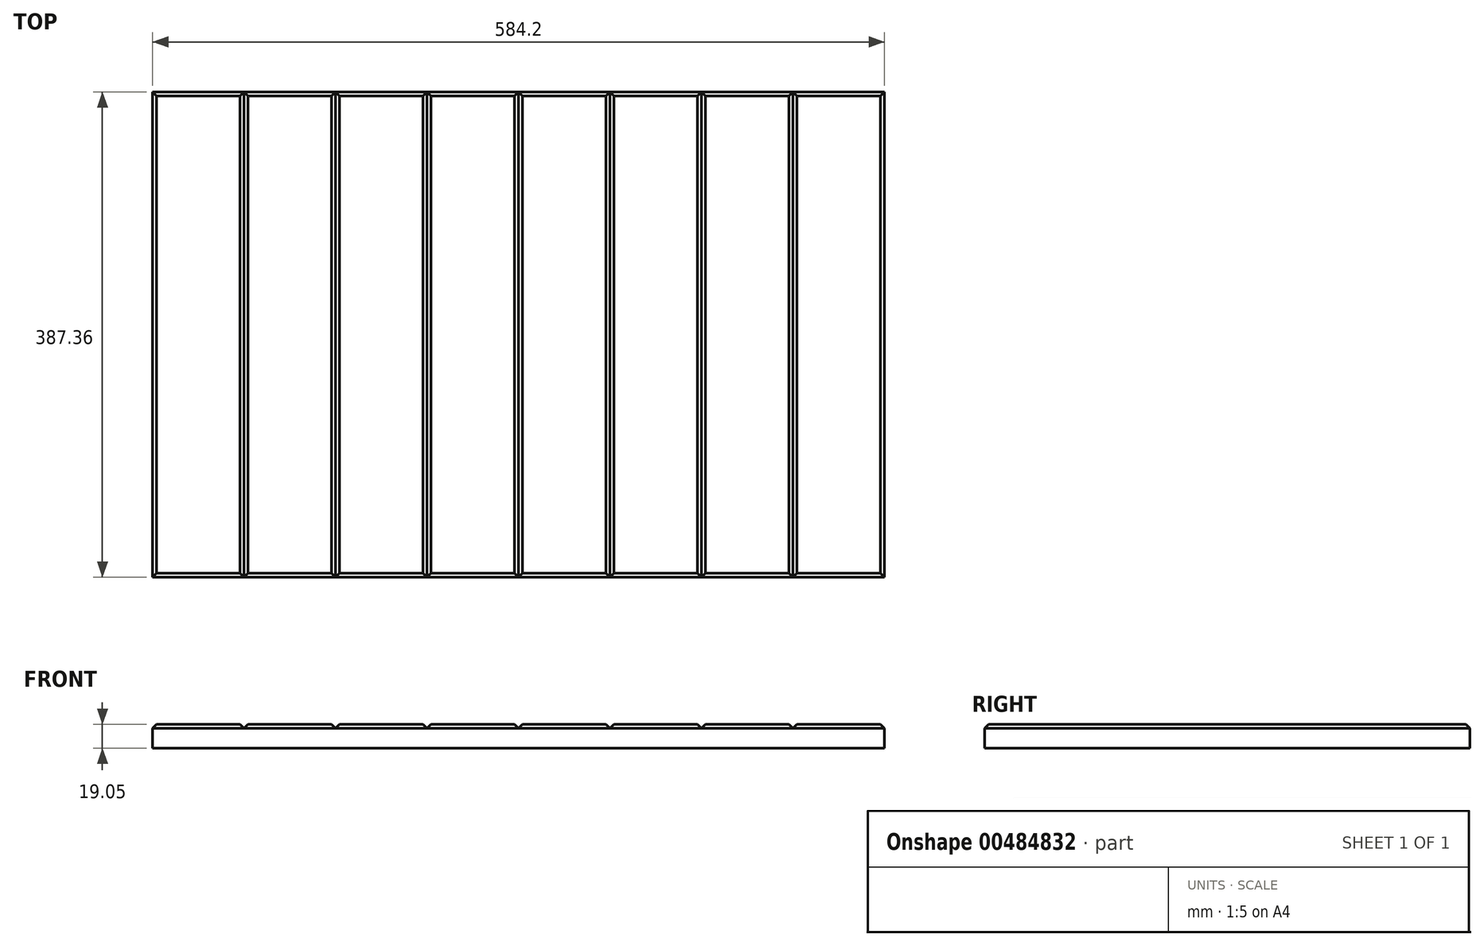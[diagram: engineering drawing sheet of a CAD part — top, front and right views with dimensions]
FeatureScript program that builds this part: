
annotation { "Feature Type Name" : "Feature", "Feature Type Description" : "" }
export const myFeature = defineFeature(function(context is Context, id is Id, definition is map)
    precondition{}
    {
        {
            var Q0;
            Q0=qCreatedBy(makeId("Top.planeOp"),FACE);
            var sketch = newSketch(context, id + "F0", { "sketchPlane" : qUnion([Q0])});
            skLineSegment(sketch, "E0.bottom", {"start": v(-292.1, 193.67) * mm, "end": v(292.1, 193.67) * mm});
            skLineSegment(sketch, "E0.top", {"start": v(-292.1, -193.68) * mm, "end": v(292.1, -193.68) * mm});
            skLineSegment(sketch, "E0.left", {"start": v(-292.1, 193.67) * mm, "end": v(-292.1, -193.68) * mm});
            skLineSegment(sketch, "E0.right", {"start": v(292.1, 193.67) * mm, "end": v(292.1, -193.68) * mm});
            skPoint(sketch, "E0.middle", {"position": v(0, 0) * mm});
            skSolve(sketch);
        }
        {
            var Q0;
            Q0 = qSketchRegion(id + "F0", true);
            extrude(context, id + "F1", {"entities" : qUnion([Q0]), "depth" : 19.05 * mm});
        }
        {
            var Q0;
            Q0=makeQuery(id+"F1.opExtrude","SWEPT_FACE",FACE,{"disambiguationData":[OSD([sQuery(id+"F0.wireOp",EDGE,"E0.top")])]});
            var sketch = newSketch(context, id + "F2", { "sketchPlane" : qUnion([Q0])});
            skLineSegment(sketch, "E1", {"start": v(-292.1, 19.05) * mm, "end": v(-219.08, 19.05) * mm});
            skLineSegment(sketch, "E2", {"start": v(-219.08, 19.05) * mm, "end": v(-222.25, 19.05) * mm});
            skLineSegment(sketch, "E3", {"start": v(-222.25, 19.05) * mm, "end": v(-215.9, 19.05) * mm});
            skLineSegment(sketch, "E4", {"start": v(-219.08, 15.88) * mm, "end": v(-215.9, 19.05) * mm});
            skLineSegment(sketch, "E5", {"start": v(-219.08, 15.87) * mm, "end": v(-222.25, 19.05) * mm});
            skLineSegment(sketch, "E6.1.0.0", {"start": v(-149.23, 19.05) * mm, "end": v(-142.88, 19.05) * mm});
            skLineSegment(sketch, "E6.1.0.1", {"start": v(-146.05, 15.87) * mm, "end": v(-149.23, 19.05) * mm});
            skLineSegment(sketch, "E6.1.0.2", {"start": v(-146.05, 15.88) * mm, "end": v(-142.88, 19.05) * mm});
            skLineSegment(sketch, "E6.1.0.3", {"start": v(-146.05, 19.05) * mm, "end": v(-149.23, 19.05) * mm});
            skLineSegment(sketch, "E6.2.0.0", {"start": v(-76.2, 19.05) * mm, "end": v(-69.85, 19.05) * mm});
            skLineSegment(sketch, "E6.2.0.1", {"start": v(-73.03, 15.87) * mm, "end": v(-76.2, 19.05) * mm});
            skLineSegment(sketch, "E6.2.0.2", {"start": v(-73.03, 15.88) * mm, "end": v(-69.85, 19.05) * mm});
            skLineSegment(sketch, "E6.2.0.3", {"start": v(-73.03, 19.05) * mm, "end": v(-76.2, 19.05) * mm});
            skLineSegment(sketch, "E6.3.0.0", {"start": v(-3.18, 19.05) * mm, "end": v(3.17, 19.05) * mm});
            skLineSegment(sketch, "E6.3.0.1", {"start": v(0, 15.87) * mm, "end": v(-3.18, 19.05) * mm});
            skLineSegment(sketch, "E6.3.0.2", {"start": v(0, 15.88) * mm, "end": v(3.17, 19.05) * mm});
            skLineSegment(sketch, "E6.3.0.3", {"start": v(0, 19.05) * mm, "end": v(-3.18, 19.05) * mm});
            skLineSegment(sketch, "E6.4.0.0", {"start": v(69.85, 19.05) * mm, "end": v(76.2, 19.05) * mm});
            skLineSegment(sketch, "E6.4.0.1", {"start": v(73.03, 15.87) * mm, "end": v(69.85, 19.05) * mm});
            skLineSegment(sketch, "E6.4.0.2", {"start": v(73.03, 15.88) * mm, "end": v(76.2, 19.05) * mm});
            skLineSegment(sketch, "E6.4.0.3", {"start": v(73.03, 19.05) * mm, "end": v(69.85, 19.05) * mm});
            skLineSegment(sketch, "E6.5.0.0", {"start": v(142.88, 19.05) * mm, "end": v(149.22, 19.05) * mm});
            skLineSegment(sketch, "E6.5.0.1", {"start": v(146.05, 15.87) * mm, "end": v(142.88, 19.05) * mm});
            skLineSegment(sketch, "E6.5.0.2", {"start": v(146.05, 15.88) * mm, "end": v(149.22, 19.05) * mm});
            skLineSegment(sketch, "E6.5.0.3", {"start": v(146.05, 19.05) * mm, "end": v(142.88, 19.05) * mm});
            skLineSegment(sketch, "E6.6.0.0", {"start": v(215.9, 19.05) * mm, "end": v(222.25, 19.05) * mm});
            skLineSegment(sketch, "E6.6.0.1", {"start": v(219.08, 15.87) * mm, "end": v(215.9, 19.05) * mm});
            skLineSegment(sketch, "E6.6.0.2", {"start": v(219.08, 15.88) * mm, "end": v(222.25, 19.05) * mm});
            skLineSegment(sketch, "E6.6.0.3", {"start": v(219.08, 19.05) * mm, "end": v(215.9, 19.05) * mm});
            skSolve(sketch);
        }
        {
            var Q0;
            Q0 = qSketchRegion(id + "F2", true);
            extrude(context, id + "F3", {"entities" : qUnion([Q0]), "operationType" : NewBodyOperationType.REMOVE, "endBound" : BoundingType.THROUGH_ALL, "oppositeDirection" : true, "depth" : 25.4 * mm});
        }
        {
            var Q0;
            Q0=makeQuery(id+"F1.opExtrude","CAP_EDGE",EDGE,{"disambiguationData":[OSD([sQuery(id+"F0.wireOp",EDGE,"E0.left")])],"isStart":false});
            var Q1;
            {var subQ0=sQuery(id+"F0.wireOp",EDGE,"E0.left");var subQ1=sQuery(id+"F0.wireOp",EDGE,"E0.top");Q1=makeQuery(id+"F3.boolean.opBoolean","SPLIT",EDGE,{"disambiguationData":[TD([makeQuery(id+"F1.opExtrude","SWEPT_FACE",FACE,{"disambiguationData":[OSD([subQ0])]})])],"derivedFrom":makeQuery(id+"F1.opExtrude","CAP_EDGE",EDGE,{"disambiguationData":[OSD([subQ1])],"isStart":false})});}
            var Q2;
            {var subQ0=sQuery(id+"F0.wireOp",EDGE,"E0.top");Q2=makeQuery(id+"F3.boolean.opBoolean","SPLIT",EDGE,{"disambiguationData":[TD([makeQuery(id+"F3.opExtrude","SWEPT_FACE",FACE,{"disambiguationData":[OSD([sQuery(id+"F2.wireOp",EDGE,"E4")])]})])],"derivedFrom":makeQuery(id+"F1.opExtrude","CAP_EDGE",EDGE,{"disambiguationData":[OSD([subQ0])],"isStart":false})});}
            var Q3;
            {var subQ0=sQuery(id+"F0.wireOp",EDGE,"E0.top");Q3=makeQuery(id+"F3.boolean.opBoolean","SPLIT",EDGE,{"disambiguationData":[TD([makeQuery(id+"F3.opExtrude","SWEPT_FACE",FACE,{"disambiguationData":[OSD([sQuery(id+"F2.wireOp",EDGE,"E6.1.0.2")])]})])],"derivedFrom":makeQuery(id+"F1.opExtrude","CAP_EDGE",EDGE,{"disambiguationData":[OSD([subQ0])],"isStart":false})});}
            var Q4;
            {var subQ0=sQuery(id+"F0.wireOp",EDGE,"E0.top");Q4=makeQuery(id+"F3.boolean.opBoolean","SPLIT",EDGE,{"disambiguationData":[TD([makeQuery(id+"F3.opExtrude","SWEPT_FACE",FACE,{"disambiguationData":[OSD([sQuery(id+"F2.wireOp",EDGE,"E6.2.0.2")])]})])],"derivedFrom":makeQuery(id+"F1.opExtrude","CAP_EDGE",EDGE,{"disambiguationData":[OSD([subQ0])],"isStart":false})});}
            var Q5;
            {var subQ0=sQuery(id+"F0.wireOp",EDGE,"E0.top");Q5=makeQuery(id+"F3.boolean.opBoolean","SPLIT",EDGE,{"disambiguationData":[TD([makeQuery(id+"F3.opExtrude","SWEPT_FACE",FACE,{"disambiguationData":[OSD([sQuery(id+"F2.wireOp",EDGE,"E6.3.0.2")])]})])],"derivedFrom":makeQuery(id+"F1.opExtrude","CAP_EDGE",EDGE,{"disambiguationData":[OSD([subQ0])],"isStart":false})});}
            var Q6;
            {var subQ0=sQuery(id+"F0.wireOp",EDGE,"E0.top");Q6=makeQuery(id+"F3.boolean.opBoolean","SPLIT",EDGE,{"disambiguationData":[TD([makeQuery(id+"F3.opExtrude","SWEPT_FACE",FACE,{"disambiguationData":[OSD([sQuery(id+"F2.wireOp",EDGE,"E6.4.0.2")])]})])],"derivedFrom":makeQuery(id+"F1.opExtrude","CAP_EDGE",EDGE,{"disambiguationData":[OSD([subQ0])],"isStart":false})});}
            var Q7;
            {var subQ0=sQuery(id+"F0.wireOp",EDGE,"E0.top");Q7=makeQuery(id+"F3.boolean.opBoolean","SPLIT",EDGE,{"disambiguationData":[TD([makeQuery(id+"F3.opExtrude","SWEPT_FACE",FACE,{"disambiguationData":[OSD([sQuery(id+"F2.wireOp",EDGE,"E6.5.0.2")])]})])],"derivedFrom":makeQuery(id+"F1.opExtrude","CAP_EDGE",EDGE,{"disambiguationData":[OSD([subQ0])],"isStart":false})});}
            var Q8;
            {var subQ0=sQuery(id+"F0.wireOp",EDGE,"E0.right");var subQ1=sQuery(id+"F0.wireOp",EDGE,"E0.top");Q8=makeQuery(id+"F3.boolean.opBoolean","SPLIT",EDGE,{"disambiguationData":[TD([makeQuery(id+"F1.opExtrude","SWEPT_FACE",FACE,{"disambiguationData":[OSD([subQ0])]})])],"derivedFrom":makeQuery(id+"F1.opExtrude","CAP_EDGE",EDGE,{"disambiguationData":[OSD([subQ1])],"isStart":false})});}
            var Q9;
            {var subQ0=sQuery(id+"F0.wireOp",EDGE,"E0.bottom");var subQ1=sQuery(id+"F0.wireOp",EDGE,"E0.right");Q9=makeQuery(id+"F3.boolean.opBoolean","SPLIT",EDGE,{"disambiguationData":[TD([makeQuery(id+"F1.opExtrude","SWEPT_FACE",FACE,{"disambiguationData":[OSD([subQ1])]})])],"derivedFrom":makeQuery(id+"F1.opExtrude","CAP_EDGE",EDGE,{"disambiguationData":[OSD([subQ0])],"isStart":false})});}
            var Q10;
            {var subQ0=sQuery(id+"F0.wireOp",EDGE,"E0.bottom");Q10=makeQuery(id+"F3.boolean.opBoolean","SPLIT",EDGE,{"disambiguationData":[TD([makeQuery(id+"F3.opExtrude","SWEPT_FACE",FACE,{"disambiguationData":[OSD([sQuery(id+"F2.wireOp",EDGE,"E6.5.0.2")])]})])],"derivedFrom":makeQuery(id+"F1.opExtrude","CAP_EDGE",EDGE,{"disambiguationData":[OSD([subQ0])],"isStart":false})});}
            var Q11;
            {var subQ0=sQuery(id+"F0.wireOp",EDGE,"E0.bottom");Q11=makeQuery(id+"F3.boolean.opBoolean","SPLIT",EDGE,{"disambiguationData":[TD([makeQuery(id+"F3.opExtrude","SWEPT_FACE",FACE,{"disambiguationData":[OSD([sQuery(id+"F2.wireOp",EDGE,"E6.4.0.2")])]})])],"derivedFrom":makeQuery(id+"F1.opExtrude","CAP_EDGE",EDGE,{"disambiguationData":[OSD([subQ0])],"isStart":false})});}
            var Q12;
            {var subQ0=sQuery(id+"F0.wireOp",EDGE,"E0.bottom");Q12=makeQuery(id+"F3.boolean.opBoolean","SPLIT",EDGE,{"disambiguationData":[TD([makeQuery(id+"F3.opExtrude","SWEPT_FACE",FACE,{"disambiguationData":[OSD([sQuery(id+"F2.wireOp",EDGE,"E6.3.0.2")])]})])],"derivedFrom":makeQuery(id+"F1.opExtrude","CAP_EDGE",EDGE,{"disambiguationData":[OSD([subQ0])],"isStart":false})});}
            var Q13;
            {var subQ0=sQuery(id+"F0.wireOp",EDGE,"E0.bottom");Q13=makeQuery(id+"F3.boolean.opBoolean","SPLIT",EDGE,{"disambiguationData":[TD([makeQuery(id+"F3.opExtrude","SWEPT_FACE",FACE,{"disambiguationData":[OSD([sQuery(id+"F2.wireOp",EDGE,"E6.2.0.2")])]})])],"derivedFrom":makeQuery(id+"F1.opExtrude","CAP_EDGE",EDGE,{"disambiguationData":[OSD([subQ0])],"isStart":false})});}
            var Q14;
            {var subQ0=sQuery(id+"F0.wireOp",EDGE,"E0.bottom");Q14=makeQuery(id+"F3.boolean.opBoolean","SPLIT",EDGE,{"disambiguationData":[TD([makeQuery(id+"F3.opExtrude","SWEPT_FACE",FACE,{"disambiguationData":[OSD([sQuery(id+"F2.wireOp",EDGE,"E6.1.0.2")])]})])],"derivedFrom":makeQuery(id+"F1.opExtrude","CAP_EDGE",EDGE,{"disambiguationData":[OSD([subQ0])],"isStart":false})});}
            var Q15;
            {var subQ0=sQuery(id+"F0.wireOp",EDGE,"E0.bottom");Q15=makeQuery(id+"F3.boolean.opBoolean","SPLIT",EDGE,{"disambiguationData":[TD([makeQuery(id+"F3.opExtrude","SWEPT_FACE",FACE,{"disambiguationData":[OSD([sQuery(id+"F2.wireOp",EDGE,"E4")])]})])],"derivedFrom":makeQuery(id+"F1.opExtrude","CAP_EDGE",EDGE,{"disambiguationData":[OSD([subQ0])],"isStart":false})});}
            var Q16;
            {var subQ0=sQuery(id+"F0.wireOp",EDGE,"E0.bottom");var subQ1=sQuery(id+"F0.wireOp",EDGE,"E0.left");Q16=makeQuery(id+"F3.boolean.opBoolean","SPLIT",EDGE,{"disambiguationData":[TD([makeQuery(id+"F1.opExtrude","SWEPT_FACE",FACE,{"disambiguationData":[OSD([subQ1])]})])],"derivedFrom":makeQuery(id+"F1.opExtrude","CAP_EDGE",EDGE,{"disambiguationData":[OSD([subQ0])],"isStart":false})});}
            var Q17;
            Q17=makeQuery(id+"F1.opExtrude","CAP_EDGE",EDGE,{"disambiguationData":[OSD([sQuery(id+"F0.wireOp",EDGE,"E0.right")])],"isStart":false});
            chamfer(context, id + "F4", {"entities" : qUnion([Q0, Q1, Q2, Q3, Q4, Q5, Q6, Q7, Q8, Q9, Q10, Q11, Q12, Q13, Q14, Q15, Q16, Q17]), "width" : 3.17 * mm, "tangentPropagation" : true});
        }
    });
